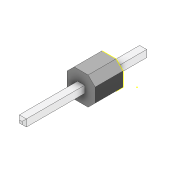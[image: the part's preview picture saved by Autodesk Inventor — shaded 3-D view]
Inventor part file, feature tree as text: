
AUTODESK INVENTOR PART (.ipt)
format: ipt  version: 2022 (Build 260153000, 153)  size: 136,704 bytes
history: mixed  units: in
note: dims shown in document units (in); Inventor stores cm internally (conversion verified against a paired STEP export)
features: sketch x2, extrude x1, projected_geometry x1, imported_body x1
ambient origin geometry x8: Origin, YZ Plane, XZ Plane, XY Plane, X Axis, Y Axis, Z Axis, Center Point
bodies: Solid1 (imported_parasolid), Body1 (imported_parasolid)
feature tree (5):
  extrude  "Extrusion1"  [1 undecoded]
  sketch  "Sketch2"
  sketch  "Sketch1"  dims[d0=0.3937in d1=0.0in]
  projected_geometry  "Projected Loop1"
  imported_body  NMx_Import_Brep_tag  [imported B-rep: ~28 faces, bbox_mm=[2.54, 2.54, 11.34]]
note: 1 required parameter value undecoded (feature->parameter linkage not recoverable at this tier; creation-order binding heuristic only, values carry confidence <= 0.55)
